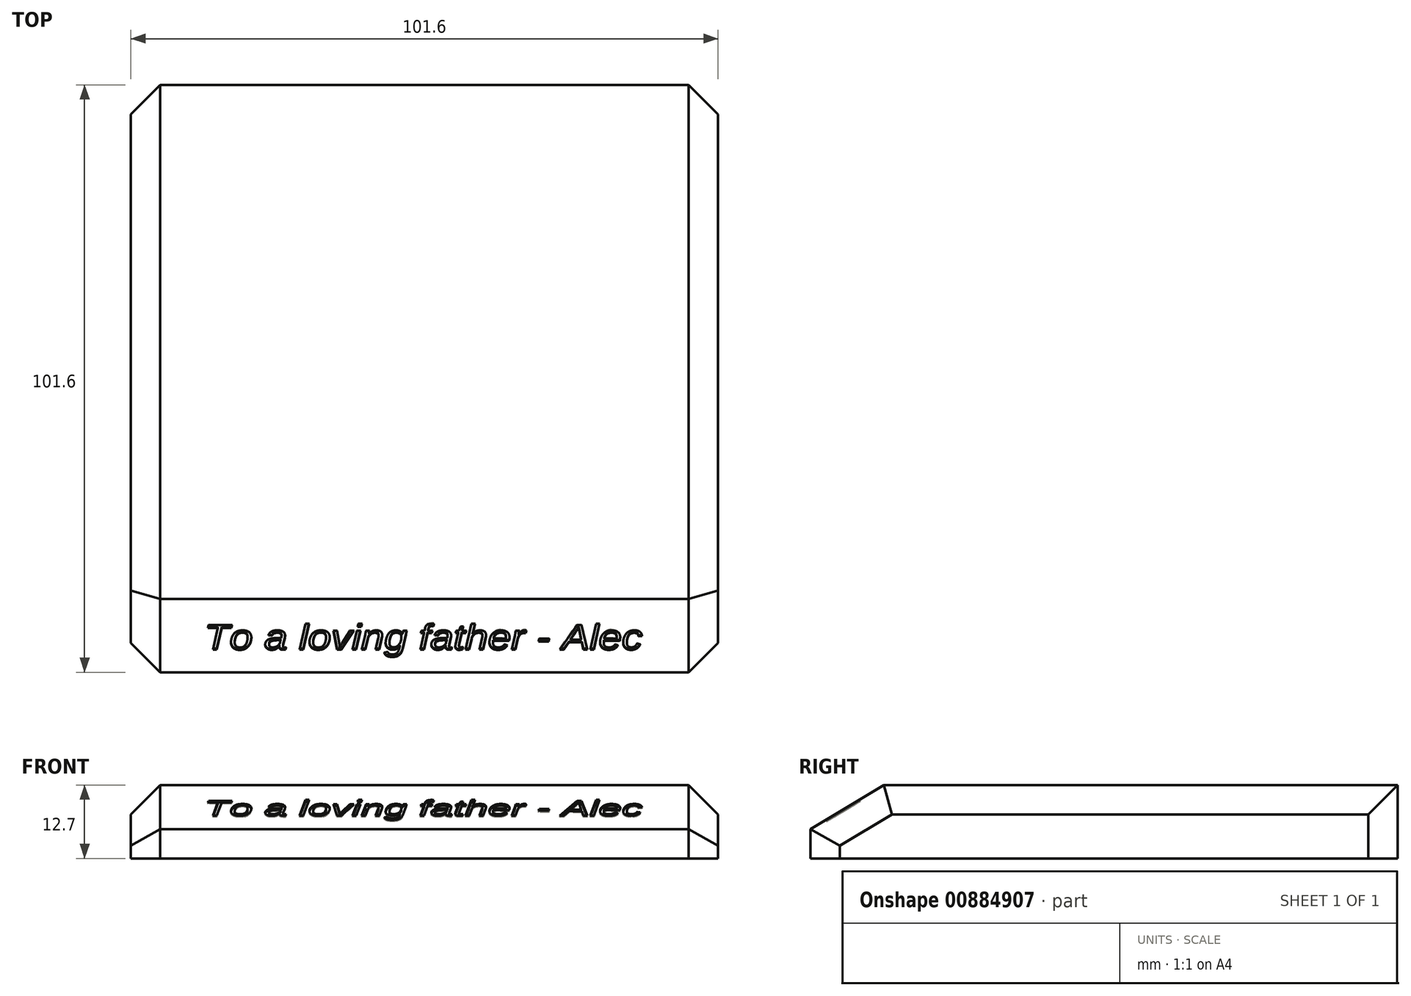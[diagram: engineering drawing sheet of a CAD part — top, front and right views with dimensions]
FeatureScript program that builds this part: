
annotation { "Feature Type Name" : "Feature", "Feature Type Description" : "" }
export const myFeature = defineFeature(function(context is Context, id is Id, definition is map)
    precondition{}
    {
        {
            var Q0;
            Q0=qCreatedBy(makeId("Top.planeOp"),FACE);
            var sketch = newSketch(context, id + "F0", { "sketchPlane" : qUnion([Q0])});
            skLineSegment(sketch, "E0.bottom", {"start": v(50.8, 50.8) * mm, "end": v(-50.8, 50.8) * mm});
            skLineSegment(sketch, "E0.top", {"start": v(50.8, -50.8) * mm, "end": v(-50.8, -50.8) * mm});
            skLineSegment(sketch, "E0.left", {"start": v(50.8, 50.8) * mm, "end": v(50.8, -50.8) * mm});
            skLineSegment(sketch, "E0.right", {"start": v(-50.8, 50.8) * mm, "end": v(-50.8, -50.8) * mm});
            skPoint(sketch, "E0.middle", {"position": v(0, 0) * mm});
            skSolve(sketch);
        }
        {
            var Q0;
            Q0=makeQuery(id+"F0.imprint","IMPRINT",FACE,{"disambiguationData":[TD([[makeQuery(id+"F0.imprint","IMPRINT",EDGE,{"derivedFrom":sQuery(id+"F0.wireOp",EDGE,"E0.bottom")}),1.0]])]});
            extrude(context, id + "F1", {"entities" : qUnion([Q0]), "depth" : 12.7 * mm, "offsetDistance" : 25.4 * mm});
        }
        {
            var Q0;
            Q0=makeQuery(id+"F1.opExtrude","CAP_EDGE",EDGE,{"disambiguationData":[OSD([sQuery(id+"F0.wireOp",EDGE,"E0.top")])],"isStart":false});
            chamfer(context, id + "F2", {"entities" : qUnion([Q0]), "chamferType" : ChamferType.TWO_OFFSETS, "width1" : 7.62 * mm, "oppositeDirection" : false, "width2" : 12.7 * mm, "tangentPropagation" : true});
        }
        {
            var Q0;
            Q0=makeQuery(id+"F1.opExtrude","SWEPT_EDGE",EDGE,{"disambiguationData":[OSD([sQuery(id+"F0.wireOp",EDGE,"E0.top"),sQuery(id+"F0.wireOp",EDGE,"E0.right")])]});
            var Q1;
            Q1=makeQuery(id+"F2.opChamfer","BLEND_EDGE",EDGE,{"blendedFrom":[makeQuery(id+"F1.opExtrude","CAP_EDGE",EDGE,{"disambiguationData":[OSD([sQuery(id+"F0.wireOp",EDGE,"E0.top")])],"isStart":false}),makeQuery(id+"F1.opExtrude","SWEPT_FACE",FACE,{"disambiguationData":[OSD([sQuery(id+"F0.wireOp",EDGE,"E0.right")])]})],"blendedInto":[makeQuery(id+"F1.opExtrude","SWEPT_FACE",FACE,{"disambiguationData":[OSD([sQuery(id+"F0.wireOp",EDGE,"E0.right")])]})]});
            var Q2;
            Q2=makeQuery(id+"F1.opExtrude","CAP_EDGE",EDGE,{"disambiguationData":[OSD([sQuery(id+"F0.wireOp",EDGE,"E0.right")])],"isStart":false});
            var Q3;
            Q3=makeQuery(id+"F1.opExtrude","SWEPT_EDGE",EDGE,{"disambiguationData":[OSD([sQuery(id+"F0.wireOp",EDGE,"E0.top"),sQuery(id+"F0.wireOp",EDGE,"E0.left")])]});
            var Q4;
            Q4=makeQuery(id+"F2.opChamfer","BLEND_EDGE",EDGE,{"blendedFrom":[makeQuery(id+"F1.opExtrude","CAP_EDGE",EDGE,{"disambiguationData":[OSD([sQuery(id+"F0.wireOp",EDGE,"E0.top")])],"isStart":false}),makeQuery(id+"F1.opExtrude","SWEPT_FACE",FACE,{"disambiguationData":[OSD([sQuery(id+"F0.wireOp",EDGE,"E0.left")])]})],"blendedInto":[makeQuery(id+"F1.opExtrude","SWEPT_FACE",FACE,{"disambiguationData":[OSD([sQuery(id+"F0.wireOp",EDGE,"E0.left")])]})]});
            var Q5;
            Q5=makeQuery(id+"F1.opExtrude","CAP_EDGE",EDGE,{"disambiguationData":[OSD([sQuery(id+"F0.wireOp",EDGE,"E0.left")])],"isStart":false});
            var Q6;
            Q6=makeQuery(id+"F1.opExtrude","SWEPT_EDGE",EDGE,{"disambiguationData":[OSD([sQuery(id+"F0.wireOp",EDGE,"E0.bottom"),sQuery(id+"F0.wireOp",EDGE,"E0.left")])]});
            var Q7;
            Q7=makeQuery(id+"F1.opExtrude","SWEPT_EDGE",EDGE,{"disambiguationData":[OSD([sQuery(id+"F0.wireOp",EDGE,"E0.bottom"),sQuery(id+"F0.wireOp",EDGE,"E0.right")])]});
            chamfer(context, id + "F3", {"entities" : qUnion([Q0, Q1, Q2, Q3, Q4, Q5, Q6, Q7]), "width" : 5.08 * mm, "tangentPropagation" : true});
        }
        {
            var Q0;
            Q0=makeQuery(id+"F2.opChamfer","BLEND_FACE",FACE,{"disambiguationData":[OSD([sQuery(id+"F0.wireOp",EDGE,"E0.top")])]});
            var sketch = newSketch(context, id + "F4", { "sketchPlane" : qUnion([Q0])});
            skText(sketch, "E1", { "text": "To a loving father - Alec", "fontName": "Arimo-Italic.ttf"});
            const initialGuessF4  = {"E1": [-0.0381, -0.03638, 1, 0, 0.00517]};
            skSetInitialGuess(sketch, initialGuessF4);
            skSolve(sketch);
        }
        {
            var Q0;
            Q0 = qSketchRegion(id + "F4", true);
            extrude(context, id + "F5", {"entities" : qUnion([Q0]), "operationType" : NewBodyOperationType.REMOVE, "oppositeDirection" : true, "depth" : 0.3 * mm, "offsetDistance" : 25.4 * mm});
        }
    });
